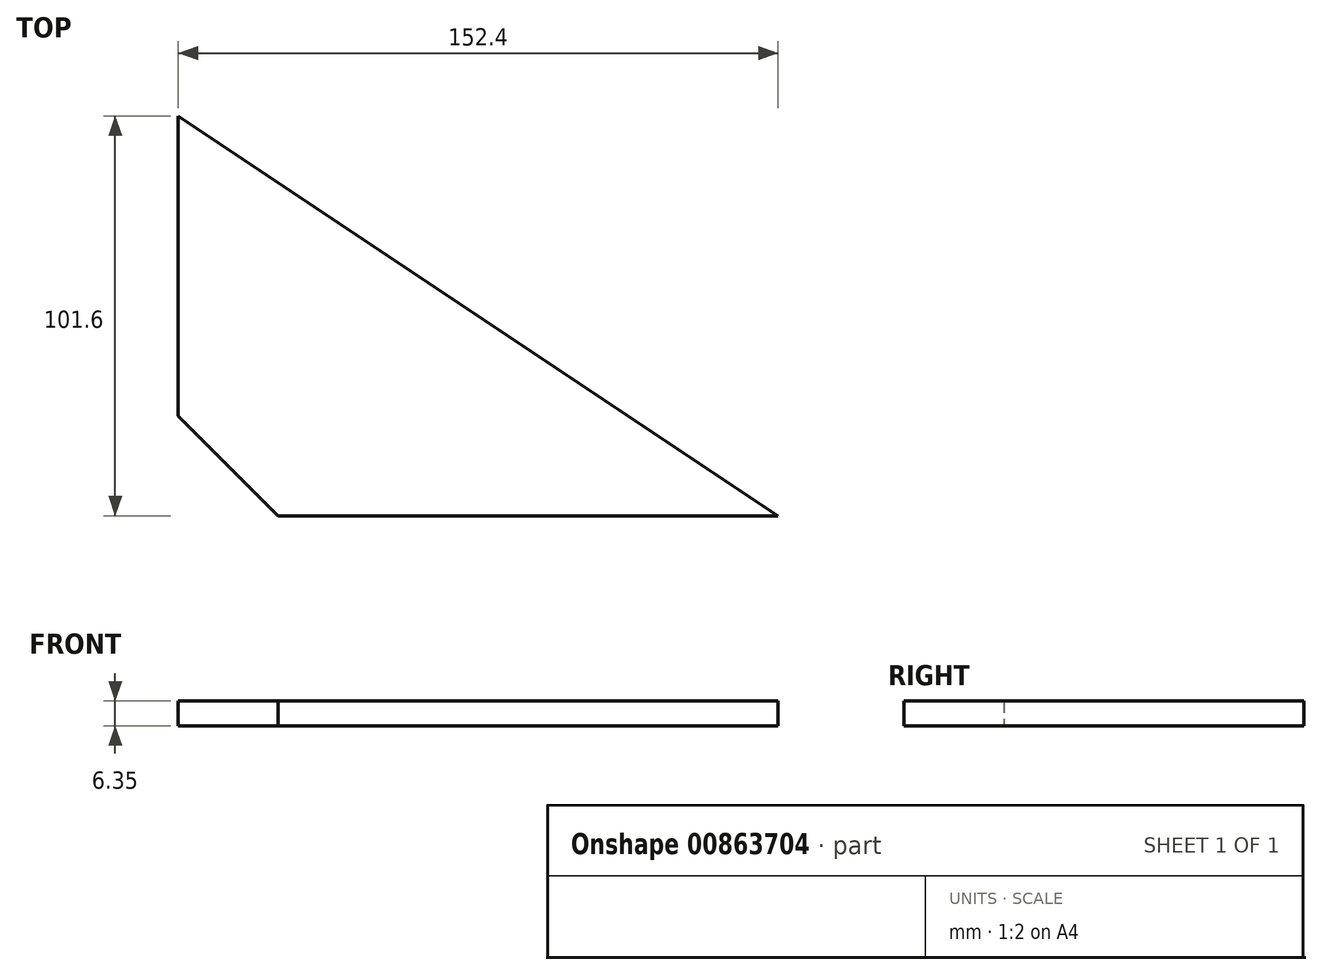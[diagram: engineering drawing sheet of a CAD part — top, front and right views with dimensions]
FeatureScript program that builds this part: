
annotation { "Feature Type Name" : "Feature", "Feature Type Description" : "" }
export const myFeature = defineFeature(function(context is Context, id is Id, definition is map)
    precondition{}
    {
        {
            var Q0;
            Q0=qCreatedBy(makeId("Top.planeOp"),FACE);
            var sketch = newSketch(context, id + "F0", { "sketchPlane" : qUnion([Q0])});
            skLineSegment(sketch, "E0", {"start": v(0, 0) * mm, "end": v(0, 101.6) * mm});
            skLineSegment(sketch, "E1", {"start": v(0, 101.6) * mm, "end": v(152.4, 0) * mm});
            skLineSegment(sketch, "E2", {"start": v(152.4, 0) * mm, "end": v(0, 0) * mm});
            skLineSegment(sketch, "E3", {"start": v(0, 25.4) * mm, "end": v(25.4, 0) * mm});
            skSolve(sketch);
        }
        {
            var Q0;
            {var subQ0=sQuery(id+"F0.wireOp",EDGE,"E1");Q0=makeQuery(id+"F0.imprint","IMPRINT",FACE,{"disambiguationData":[TD([[makeQuery(id+"F0.imprint","IMPRINT",EDGE,{"derivedFrom":subQ0}),-1.0]])]});}
            extrude(context, id + "F1", {"entities" : qUnion([Q0]), "depth" : 6.35 * mm, "offsetDistance" : 25.4 * mm});
        }
    });
